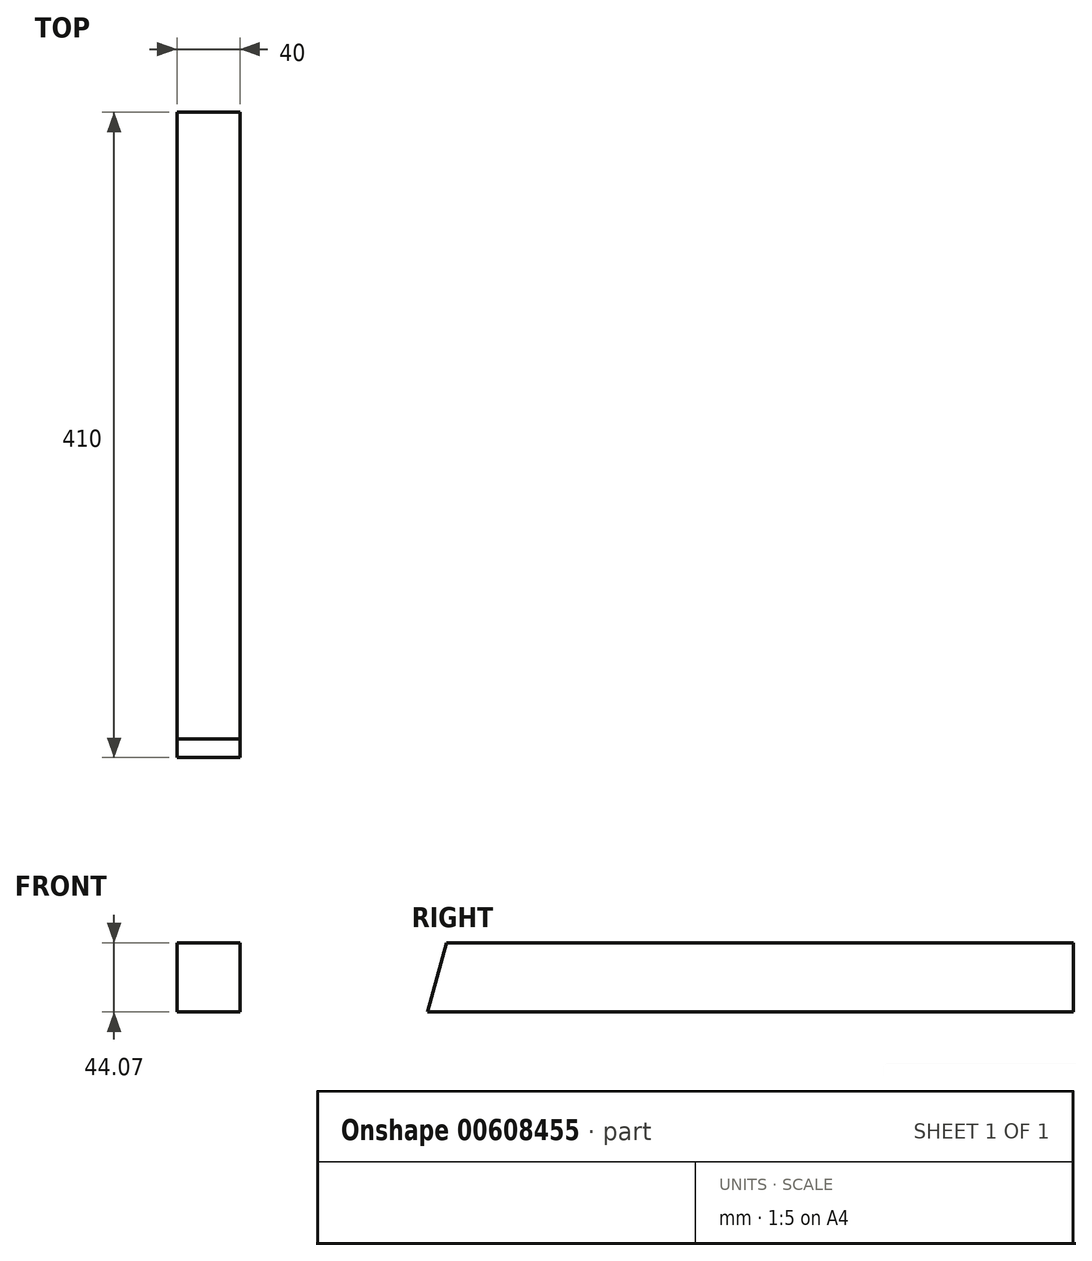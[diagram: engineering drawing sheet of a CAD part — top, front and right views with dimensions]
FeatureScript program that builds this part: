
annotation { "Feature Type Name" : "Feature", "Feature Type Description" : "" }
export const myFeature = defineFeature(function(context is Context, id is Id, definition is map)
    precondition{}
    {
        {
            var Q0;
            Q0=qCreatedBy(makeId("Right.planeOp"),FACE);
            var sketch = newSketch(context, id + "F0", { "sketchPlane" : qUnion([Q0])});
            skLineSegment(sketch, "E0.bottom", {"start": v(-71.44, 32.96) * mm, "end": v(326.75, 32.96) * mm});
            skLineSegment(sketch, "E0.top", {"start": v(-83.25, -11.1) * mm, "end": v(326.75, -11.1) * mm});
            skLineSegment(sketch, "E0.right", {"start": v(326.75, 32.96) * mm, "end": v(326.75, -11.1) * mm});
            skLineSegment(sketch, "E1", {"start": v(-83.25, -11.1) * mm, "end": v(-71.44, 32.96) * mm});
            skSolve(sketch);
        }
        {
            var Q0;
            Q0=makeQuery(id+"F0.imprint","IMPRINT",FACE,{"disambiguationData":[TD([[makeQuery(id+"F0.imprint","IMPRINT",EDGE,{"derivedFrom":sQuery(id+"F0.wireOp",EDGE,"E0.bottom")}),-1.0]])]});
            extrude(context, id + "F1", {"entities" : qUnion([Q0]), "depth" : 40 * mm, "offsetDistance" : 25 * mm});
        }
    });
